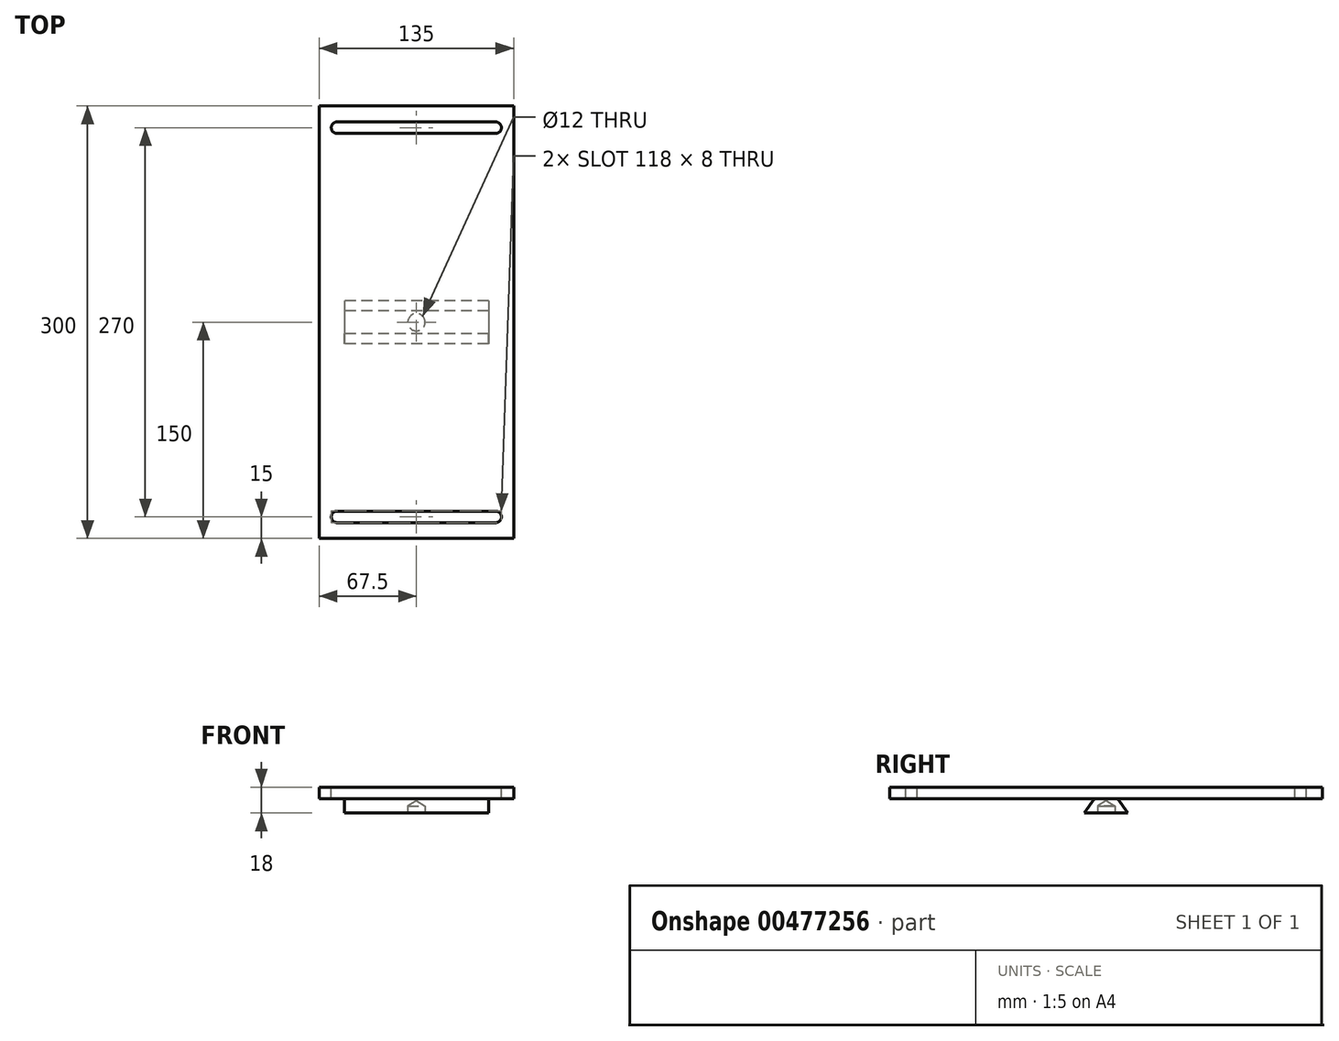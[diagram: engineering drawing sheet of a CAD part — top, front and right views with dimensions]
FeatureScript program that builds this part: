
annotation { "Feature Type Name" : "Feature", "Feature Type Description" : "" }
export const myFeature = defineFeature(function(context is Context, id is Id, definition is map)
    precondition{}
    {
        {
            var Q0;
            Q0=qCreatedBy(makeId("Top.planeOp"),FACE);
            var sketch = newSketch(context, id + "F0", { "sketchPlane" : qUnion([Q0])});
            skLineSegment(sketch, "E0.bottom", {"start": v(67.5, -150) * mm, "end": v(-67.5, -150) * mm});
            skLineSegment(sketch, "E0.top", {"start": v(67.5, 150) * mm, "end": v(-67.5, 150) * mm});
            skLineSegment(sketch, "E0.left", {"start": v(67.5, -150) * mm, "end": v(67.5, 150) * mm});
            skLineSegment(sketch, "E0.right", {"start": v(-67.5, -150) * mm, "end": v(-67.5, 150) * mm});
            skPoint(sketch, "E0.middle", {"position": v(0, 0) * mm});
            skSolve(sketch);
        }
        {
            var Q0;
            Q0=makeQuery(id+"F0.imprint","IMPRINT",FACE,{"disambiguationData":[TD([[makeQuery(id+"F0.imprint","IMPRINT",EDGE,{"derivedFrom":sQuery(id+"F0.wireOp",EDGE,"E0.bottom")}),-1.0]])]});
            extrude(context, id + "F1", {"entities" : qUnion([Q0]), "depth" : 8 * mm});
        }
        {
            var Q0;
            Q0=qCreatedBy(makeId("Right.planeOp"),FACE);
            var sketch = newSketch(context, id + "F2", { "sketchPlane" : qUnion([Q0])});
            skLineSegment(sketch, "E1", {"start": v(0, 0) * mm, "end": v(0, -10) * mm});
            skLineSegment(sketch, "E2", {"start": v(0, -10) * mm, "end": v(15, -10) * mm});
            skLineSegment(sketch, "E3", {"start": v(15, -10) * mm, "end": v(8, 0) * mm});
            skLineSegment(sketch, "E4", {"start": v(0, -10) * mm, "end": v(-15, -10) * mm});
            skLineSegment(sketch, "E5", {"start": v(-15, -10) * mm, "end": v(-8, 0) * mm});
            skLineSegment(sketch, "E6", {"start": v(8, 0) * mm, "end": v(-8, 0) * mm});
            skSolve(sketch);
        }
        {
            var Q0;
            {var subQ0=sQuery(id+"F2.wireOp",EDGE,"E1");Q0=makeQuery(id+"F2.imprint","IMPRINT",FACE,{"disambiguationData":[TD([[makeQuery(id+"F2.imprint","IMPRINT",EDGE,{"derivedFrom":subQ0}),-1.0]])]});}
            var Q1;
            {var subQ0=sQuery(id+"F2.wireOp",EDGE,"E1");Q1=makeQuery(id+"F2.imprint","IMPRINT",FACE,{"disambiguationData":[TD([[makeQuery(id+"F2.imprint","IMPRINT",EDGE,{"derivedFrom":subQ0}),1.0]])]});}
            extrude(context, id + "F3", {"entities" : qUnion([Q0, Q1]), "operationType" : NewBodyOperationType.ADD, "endBound" : BoundingType.SYMMETRIC, "depth" : 100 * mm});
        }
        {
            var Q0;
            Q0=makeQuery(id+"F3.opExtrude","SWEPT_FACE",FACE,{"disambiguationData":[OSD([sQuery(id+"F2.wireOp",EDGE,"E2"),sQuery(id+"F2.wireOp",EDGE,"E4")])]});
            var sketch = newSketch(context, id + "F4", { "sketchPlane" : qUnion([Q0])});
            skPoint(sketch, "E7", {"position": v(0, 0) * mm});
            skSolve(sketch);
        }
        {
            var Q0;
            Q0=sQuery(id+"F4.wireOp",VERTEX,"E7");
            var Q1;
            Q1=makeQuery(id+"F1.opExtrude","SWEPT_BODY",BODY,{"disambiguationData":[OSD([sQuery(id+"F0.wireOp",EDGE,"E0.bottom"),sQuery(id+"F0.wireOp",EDGE,"E0.top"),sQuery(id+"F0.wireOp",EDGE,"E0.left"),sQuery(id+"F0.wireOp",EDGE,"E0.right")])]});
            hole(context, id + "F5", {"style" : HoleStyle.SIMPLE, "endStyle" : HoleEndStyle.BLIND, "holeDiameter" : 12 * mm, "holeDepth" : 5 * mm, "isTappedThrough" : true, "tappedDepth" : 12 * mm, "tapClearance" : 3, "locations" : qUnion([Q0]), "scope" : qUnion([Q1])});
        }
        {
            var Q0;
            Q0=makeQuery(id+"F1.opExtrude","CAP_FACE",FACE,{"disambiguationData":[OSD([sQuery(id+"F0.wireOp",EDGE,"E0.bottom"),sQuery(id+"F0.wireOp",EDGE,"E0.top"),sQuery(id+"F0.wireOp",EDGE,"E0.left"),sQuery(id+"F0.wireOp",EDGE,"E0.right")])],"isStart":false});
            var sketch = newSketch(context, id + "F6", { "sketchPlane" : qUnion([Q0])});
            skLineSegment(sketch, "E8.bottom", {"start": v(-55, -131) * mm, "end": v(55, -131) * mm});
            skLineSegment(sketch, "E8.top", {"start": v(-55, -139) * mm, "end": v(55, -139) * mm});
            skLineSegment(sketch, "E8.left", {"start": v(-55, -131) * mm, "end": v(-55, -139) * mm});
            skLineSegment(sketch, "E8.right", {"start": v(55, -131) * mm, "end": v(55, -139) * mm});
            skPoint(sketch, "E8.middle", {"position": v(0, -135) * mm});
            skCircle(sketch, "E9", {"center": v(-55, -135) * mm, "radius": 4 * mm});
            skCircle(sketch, "E10", {"center": v(55, -135) * mm, "radius": 4 * mm});
            skLineSegment(sketch, "E11.MirrorCS", {"start": v(-55, 131) * mm, "end": v(-55, 139) * mm});
            skLineSegment(sketch, "E12.MirrorCS", {"start": v(55, 131) * mm, "end": v(55, 139) * mm});
            skCircle(sketch, "E13.MirrorC", {"center": v(-55, 135) * mm, "radius": 4 * mm});
            skCircle(sketch, "E14.MirrorC", {"center": v(55, 135) * mm, "radius": 4 * mm});
            skLineSegment(sketch, "E15.MirrorCS", {"start": v(-55, 131) * mm, "end": v(55, 131) * mm});
            skLineSegment(sketch, "E16.MirrorCS", {"start": v(-55, 139) * mm, "end": v(55, 139) * mm});
            skPoint(sketch, "E17.MirrorP", {"position": v(0, 135) * mm});
            skSolve(sketch);
        }
        {
            var Q0;
            {var subQ0=sQuery(id+"F6.wireOp",EDGE,"E8.right");Q0=makeQuery(id+"F6.imprint","IMPRINT",FACE,{"disambiguationData":[TD([[makeQuery(id+"F6.imprint","IMPRINT",EDGE,{"derivedFrom":subQ0}),1.0]])]});}
            var Q1;
            {var subQ0=sQuery(id+"F6.wireOp",EDGE,"E8.right");Q1=makeQuery(id+"F6.imprint","IMPRINT",FACE,{"disambiguationData":[TD([[makeQuery(id+"F6.imprint","IMPRINT",EDGE,{"derivedFrom":subQ0}),-1.0]])]});}
            var Q2;
            {var subQ0=sQuery(id+"F6.wireOp",EDGE,"E8.bottom");Q2=makeQuery(id+"F6.imprint","IMPRINT",FACE,{"disambiguationData":[TD([[makeQuery(id+"F6.imprint","IMPRINT",EDGE,{"derivedFrom":subQ0}),-1.0]])]});}
            var Q3;
            {var subQ0=sQuery(id+"F6.wireOp",EDGE,"E8.left");Q3=makeQuery(id+"F6.imprint","IMPRINT",FACE,{"disambiguationData":[TD([[makeQuery(id+"F6.imprint","IMPRINT",EDGE,{"derivedFrom":subQ0}),1.0]])]});}
            var Q4;
            {var subQ0=sQuery(id+"F6.wireOp",EDGE,"E8.left");Q4=makeQuery(id+"F6.imprint","IMPRINT",FACE,{"disambiguationData":[TD([[makeQuery(id+"F6.imprint","IMPRINT",EDGE,{"derivedFrom":subQ0}),-1.0]])]});}
            var Q5;
            {var subQ0=sQuery(id+"F6.wireOp",EDGE,"E12.MirrorCS");Q5=makeQuery(id+"F6.imprint","IMPRINT",FACE,{"disambiguationData":[TD([[makeQuery(id+"F6.imprint","IMPRINT",EDGE,{"derivedFrom":subQ0}),-1.0]])]});}
            var Q6;
            {var subQ0=sQuery(id+"F6.wireOp",EDGE,"E12.MirrorCS");Q6=makeQuery(id+"F6.imprint","IMPRINT",FACE,{"disambiguationData":[TD([[makeQuery(id+"F6.imprint","IMPRINT",EDGE,{"derivedFrom":subQ0}),1.0]])]});}
            var Q7;
            {var subQ0=sQuery(id+"F6.wireOp",EDGE,"E15.MirrorCS");Q7=makeQuery(id+"F6.imprint","IMPRINT",FACE,{"disambiguationData":[TD([[makeQuery(id+"F6.imprint","IMPRINT",EDGE,{"derivedFrom":subQ0}),1.0]])]});}
            var Q8;
            {var subQ0=sQuery(id+"F6.wireOp",EDGE,"E11.MirrorCS");Q8=makeQuery(id+"F6.imprint","IMPRINT",FACE,{"disambiguationData":[TD([[makeQuery(id+"F6.imprint","IMPRINT",EDGE,{"derivedFrom":subQ0}),1.0]])]});}
            var Q9;
            {var subQ0=sQuery(id+"F6.wireOp",EDGE,"E11.MirrorCS");Q9=makeQuery(id+"F6.imprint","IMPRINT",FACE,{"disambiguationData":[TD([[makeQuery(id+"F6.imprint","IMPRINT",EDGE,{"derivedFrom":subQ0}),-1.0]])]});}
            extrude(context, id + "F7", {"entities" : qUnion([Q0, Q1, Q2, Q3, Q4, Q5, Q6, Q7, Q8, Q9]), "operationType" : NewBodyOperationType.REMOVE, "oppositeDirection" : true, "depth" : 25 * mm});
        }
    });
